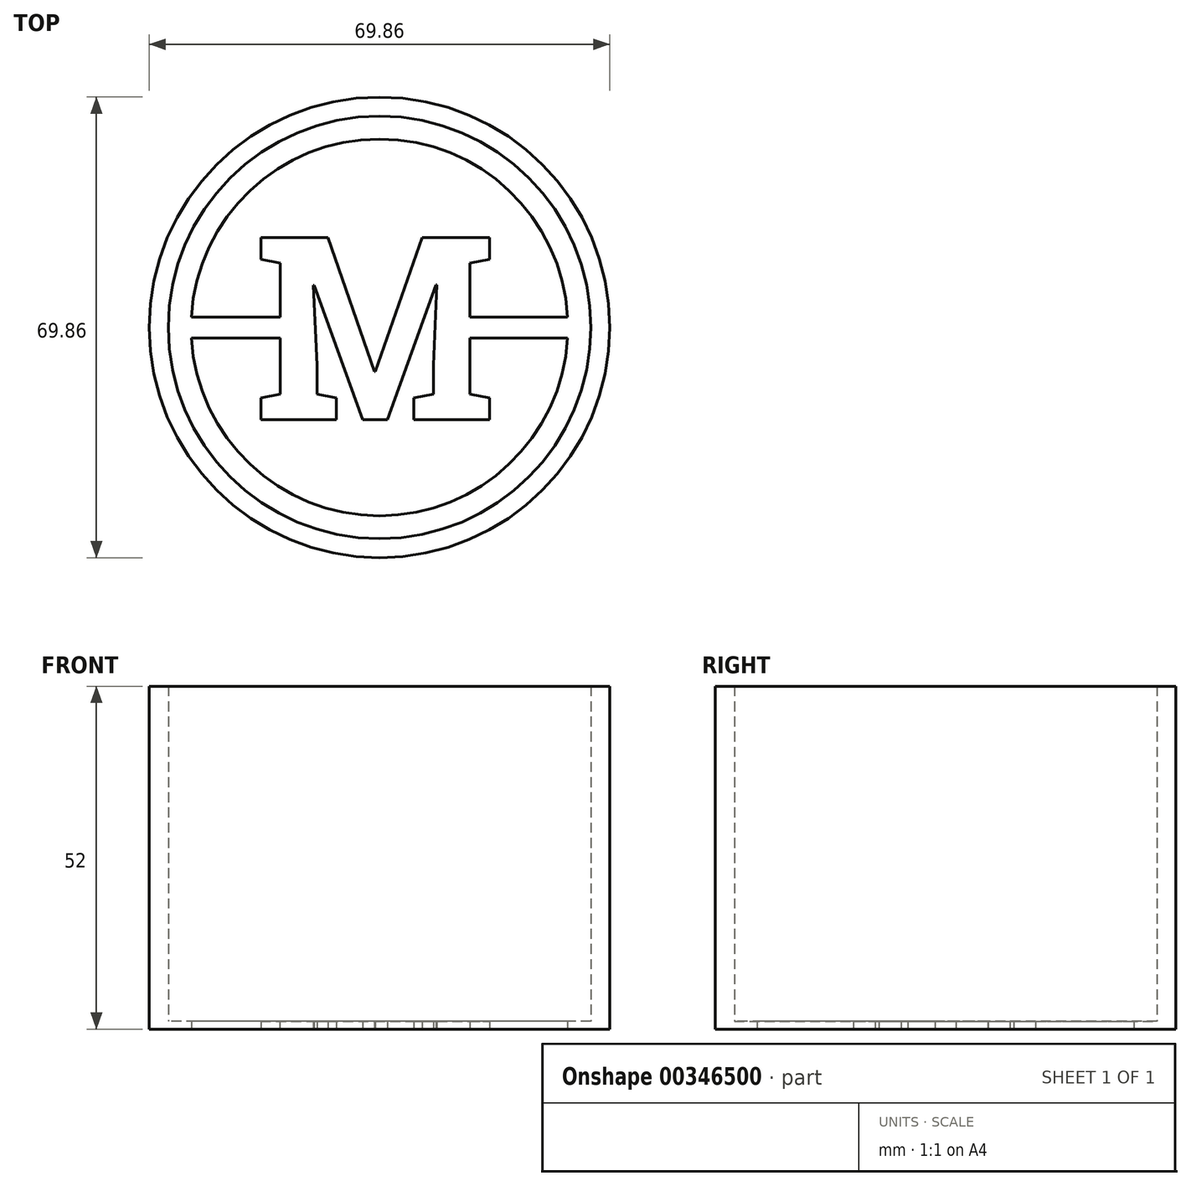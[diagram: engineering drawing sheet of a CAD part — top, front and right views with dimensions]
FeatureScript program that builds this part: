
annotation { "Feature Type Name" : "Feature", "Feature Type Description" : "" }
export const myFeature = defineFeature(function(context is Context, id is Id, definition is map)
    precondition{}
    {
        {
            var Q0;
            Q0=qCreatedBy(makeId("Top.planeOp"),FACE);
            var sketch = newSketch(context, id + "F0", { "sketchPlane" : qUnion([Q0])});
            skText(sketch, "E0", { "text": "M", "fontName": "RobotoSlab-Bold.ttf"});
            skLineSegment(sketch, "E1", {"start": v(0, 0) * mm, "end": v(19.05, 0) * mm, "construction": true});
            skCircle(sketch, "E2", {"center": v(0, 0) * mm, "radius": 34.93 * mm});
            skPoint(sketch, "E3.end.orphan", {"position": v(-28.53, 1.59) * mm});
            skPoint(sketch, "E3.start.orphan", {"position": v(-28.53, -1.59) * mm});
            skCircle(sketch, "E4", {"center": v(0, 0) * mm, "radius": 28.58 * mm});
            const initialGuessF0  = {"E0": [-0.01905, -0.014, 1, 0, 0.028]};
            skSetInitialGuess(sketch, initialGuessF0);
            skSolve(sketch);
        }
        {
            var Q0;
            Q0=qSketchRegion(id+"F0",true);
            extrude(context, id + "F1", {"entities" : qUnion([Q0]), "depth" : .2 * 6 * mm});
        }
        {
            var Q0;
            Q0=qCreatedBy(makeId("Top.planeOp"),FACE);
            var sketch = newSketch(context, id + "F2", { "sketchPlane" : qUnion([Q0])});
            skText(sketch, "E5", { "text": "M", "fontName": "RobotoSlab-Bold.ttf"});
            skLineSegment(sketch, "E6", {"start": v(0, 0) * mm, "end": v(19.05, 0) * mm, "construction": true});
            const initialGuessF2  = {"E5": [-0.01905, -0.014, 1, 0, 0.028]};
            skSetInitialGuess(sketch, initialGuessF2);
            skSolve(sketch);
        }
        {
            var Q0;
            Q0=qSketchRegion(id+"F2",true);
            var Q1;
            Q1=makeQuery(id+"F1.opExtrude","CAP_FACE",FACE,{"disambiguationData":[OSD([sQuery(id+"F0.wireOp",EDGE,"E2"),sQuery(id+"F0.wireOp",EDGE,"E4")])],"isStart":false});
            extrude(context, id + "F3", {"entities" : qUnion([Q0]), "endBound" : BoundingType.UP_TO_SURFACE, "endBoundEntityFace" : qUnion([Q1]), "depth" : 25.4 * mm});
        }
        {
            var Q0;
            Q0=qCreatedBy(makeId("Top.planeOp"),FACE);
            var sketch = newSketch(context, id + "F4", { "sketchPlane" : qUnion([Q0])});
            skArc(sketch, "E7.0", {"start": v(-28.53, 1.59) * mm, "mid": v(-28.57, 0) * mm, "end": v(-28.53, -1.59) * mm});
            skLineSegment(sketch, "E8.0", {"start": v(-15.05, -10.1) * mm, "end": v(-15.05, 9.73) * mm, "construction": true});
            skLineSegment(sketch, "E9", {"start": v(-28.53, 1.59) * mm, "end": v(-15.05, 1.59) * mm});
            skLineSegment(sketch, "E10", {"start": v(-15.05, 1.59) * mm, "end": v(-15.05, -1.59) * mm});
            skLineSegment(sketch, "E11", {"start": v(-15.05, -1.59) * mm, "end": v(-28.53, -1.59) * mm});
            skLineSegment(sketch, "E12", {"start": v(-15.05, 0) * mm, "end": v(-28.58, 0) * mm, "construction": true});
            skLineSegment(sketch, "E13", {"start": v(0, 0) * mm, "end": v(0, 25.4) * mm, "construction": true});
            skArc(sketch, "E14.MirrorCS", {"start": v(28.53, 1.59) * mm, "mid": v(28.58, 0) * mm, "end": v(28.53, -1.59) * mm});
            skLineSegment(sketch, "E15.0", {"start": v(13.7, 9.73) * mm, "end": v(13.7, -10.1) * mm, "construction": true});
            skLineSegment(sketch, "E16", {"start": v(28.53, 1.59) * mm, "end": v(13.7, 1.59) * mm});
            skLineSegment(sketch, "E17", {"start": v(28.53, -1.59) * mm, "end": v(13.7, -1.59) * mm});
            skLineSegment(sketch, "E18", {"start": v(13.7, -1.59) * mm, "end": v(13.7, 1.59) * mm});
            skSolve(sketch);
        }
        {
            var Q0;
            Q0=qSketchRegion(id+"F4",true);
            var Q1;
            Q1=makeQuery(id+"F1.opExtrude","CAP_FACE",FACE,{"disambiguationData":[OSD([sQuery(id+"F0.wireOp",EDGE,"E2"),sQuery(id+"F0.wireOp",EDGE,"E4")])],"isStart":false});
            extrude(context, id + "F5", {"entities" : qUnion([Q0]), "operationType" : NewBodyOperationType.ADD, "endBound" : BoundingType.UP_TO_SURFACE, "endBoundEntityFace" : qUnion([Q1]), "depth" : 25.4 * mm});
        }
        {
            var Q0;
            {var subQ0=sQuery(id+"F0.wireOp",EDGE,"E4");var subQ1=sQuery(id+"F0.wireOp",EDGE,"E2");Q0=makeQuery(id+"F5.boolean.opBoolean","MERGE",FACE,{"derivedFrom":[makeQuery(id+"F1.opExtrude","CAP_FACE",FACE,{"disambiguationData":[OSD([subQ1,subQ0])],"isStart":false}),makeQuery(id+"F3.opExtrude","CAP_FACE",FACE,{"disambiguationData":[OSD([subQ1,subQ0])],"isStart":false}),makeQuery(id+"F5.opExtrude","CAP_FACE",FACE,{"disambiguationData":[OSD([subQ1,subQ0]),ownerDisambiguation([makeQuery(id+"F4.imprint","IMPRINT",EDGE,{"derivedFrom":sQuery(id+"F4.wireOp",EDGE,"E7.0")})])],"isStart":false}),makeQuery(id+"F5.opExtrude","CAP_FACE",FACE,{"disambiguationData":[OSD([subQ1,subQ0]),ownerDisambiguation([makeQuery(id+"F4.imprint","IMPRINT",EDGE,{"derivedFrom":sQuery(id+"F4.wireOp",EDGE,"E14.MirrorCS")})])],"isStart":false})]});}
            var sketch = newSketch(context, id + "F6", { "sketchPlane" : qUnion([Q0])});
            skCircle(sketch, "E19.0", {"center": v(0, 0) * mm, "radius": 34.93 * mm});
            skCircle(sketch, "E20.0", {"center": v(0, 0) * mm, "radius": 32.05 * mm});
            skSolve(sketch);
        }
        {
            var Q0;
            Q0 = qSketchRegion(id + "F6", true);
            extrude(context, id + "F7", {"entities" : qUnion([Q0]), "operationType" : NewBodyOperationType.ADD, "depth" : 50.8 * mm});
        }
    });
